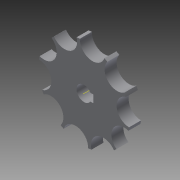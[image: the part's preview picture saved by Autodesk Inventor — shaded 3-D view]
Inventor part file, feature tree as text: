
AUTODESK INVENTOR PART (.ipt)
format: ipt  version: 2015 (Build 190159000, 159)  size: 136,704 bytes
history: native  units: mm
features: sketch x2, extrude x1, hole x1, other x1, pattern_circular x1
ambient origin geometry x8: Origin, YZ Plane, XZ Plane, XY Plane, X Axis, Y Axis, Z Axis, Center Point
bodies: Solid1 (feature_tree)
feature tree (6):
  extrude  "Extrusion1"  Depth=6.35mm
  hole  "Hole1"  [1 undecoded]
  other  "Work Axis1"
  pattern_circular  "Circular Pattern1"  [2 undecoded]
  sketch  "Sketch1"  dims[d0=12.5mm d1=6.35mm]
  sketch  "Sketch2"  dims[d2=2.4384mm d3=2.438mm d4=55.0mm d5=76.0mm d6=10.5mm d7=100.0mm d9=360.0deg d11=10.0mm d12=0.0mm d13=21.0mm d14=6.0mm d15=4.0mm d16=2.0mm d17=90.0deg d18=8.0mm d19=20.594885mm d20=100.0mm d21=360.0deg]
note: 3 required parameter values undecoded (feature->parameter linkage not recoverable at this tier; creation-order binding heuristic only, values carry confidence <= 0.55)
